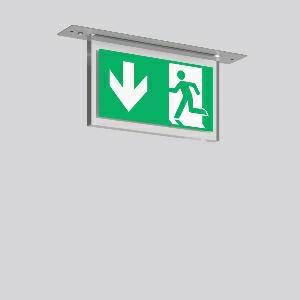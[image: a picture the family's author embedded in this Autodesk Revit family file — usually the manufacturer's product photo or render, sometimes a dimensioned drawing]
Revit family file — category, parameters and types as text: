
# Revit family: halyxx_671739_004_1_df5f
name_source: partatom
category: Lighting Fixtures
units: mm (PartAtom-declared; Revit-internal decimal feet)

## family parameters
Cut with Voids When Loaded = No
Host = Face
Light Source = No
Part Type = Normal
Room Calculation Point = No
Round Connector Dimension = Use Diameter
Shared = No

## types (1)
- HALYXX (1 x LED Modul 840, 70 lm, 4000)
    Apparent Load = 2 VA
    Approval mark = CE
    CIE Flux Codes = 18 46 76 54 100
    Color Rendering = 80
    Color Temperature = 4000
    Default Elevation = 1800 mm
    Description = Series: HALYXX
Luminaire for escape route identification. Installation housing sheet steel. Ceiling plate stainless steel high polish or powder-coated. Display panel: highly transparent panel, plastic, with legend on one side/both sides. Driver integrated. Suitable for connection to central battery systems. Please indicate legend number when placing your order! 
Colour: anodised aluminium
Length: 320 mm
Width: 55 mm
Height: 140 mm
Cut-out length: 305 mm
Cut-out width: 42 mm
Recess height: 90 mm
Weight: 1.38 kg
Operating mode: maintained power mode
Viewing Distance: 19 m
Lamp: LED
Socket: without socket
Colour temperature: 4000K
Colour rendering index (CRI): 80
System power: 2.4 W
Rated luminous flux: 70 lm
Luminous flux, emergency: 70 lm
System power, emergency: 2.2 W
Control gear: Regulated power supply
Protection class: I
Type of protection: IP 40
    Height = 0 mm  [stored 0 ft]
    Lamp = 1 x LED Modul 840
    Lamp Light Flux = 70 lm
    Lamp count = 1
    Length = 320 mm
    Lifetime = 50000 h
    Luminous efficacy = 29 lm/W
    Manufacturer = RZB
    ModVariant = No
    Model = 671739.004.1
    Mounting Place = Ceiling
    Mounting Type = Recessed
    Number of Poles = 1
    OnlyDefault = Yes
    Power Factor = 1
    Product Name = HALYXX
    Product group = Recessed ceiling luminaires
    ProductGroupID = 405
    Protection Class = Protection class I
    Protection Degree = IP 40
    RLX_Detail_Level = 1
    RLX_Emergency_Light_Flux = 0 lm
    RLX_Emergency_Type = 0
    RLX_Emergency_Type_DB = No
    RlxData = <blob elided: 39373 chars, md5=05854eb8>
    Socket = socket
    Standby Power = 0 W
    System Light Flux = 70 lm
    System Power = 2 W
    Type Comments = ALEA SPOT
    Type Image = 671750.004.jpg
    URL = http://relux.com
    VarID = ---
    Voltage = 230 V
    Voltage Range = 220-240 V
    Weight = 0.00 kg
    Width = 55 mm

note: [stored X ft] marks values corroborated as IEEE doubles in the binary element streams (Revit-internal decimal feet)

## geometry (parser evidence)
native form markers: Blend x4, Sweep x12
no freeform markers — native parametric forms only
